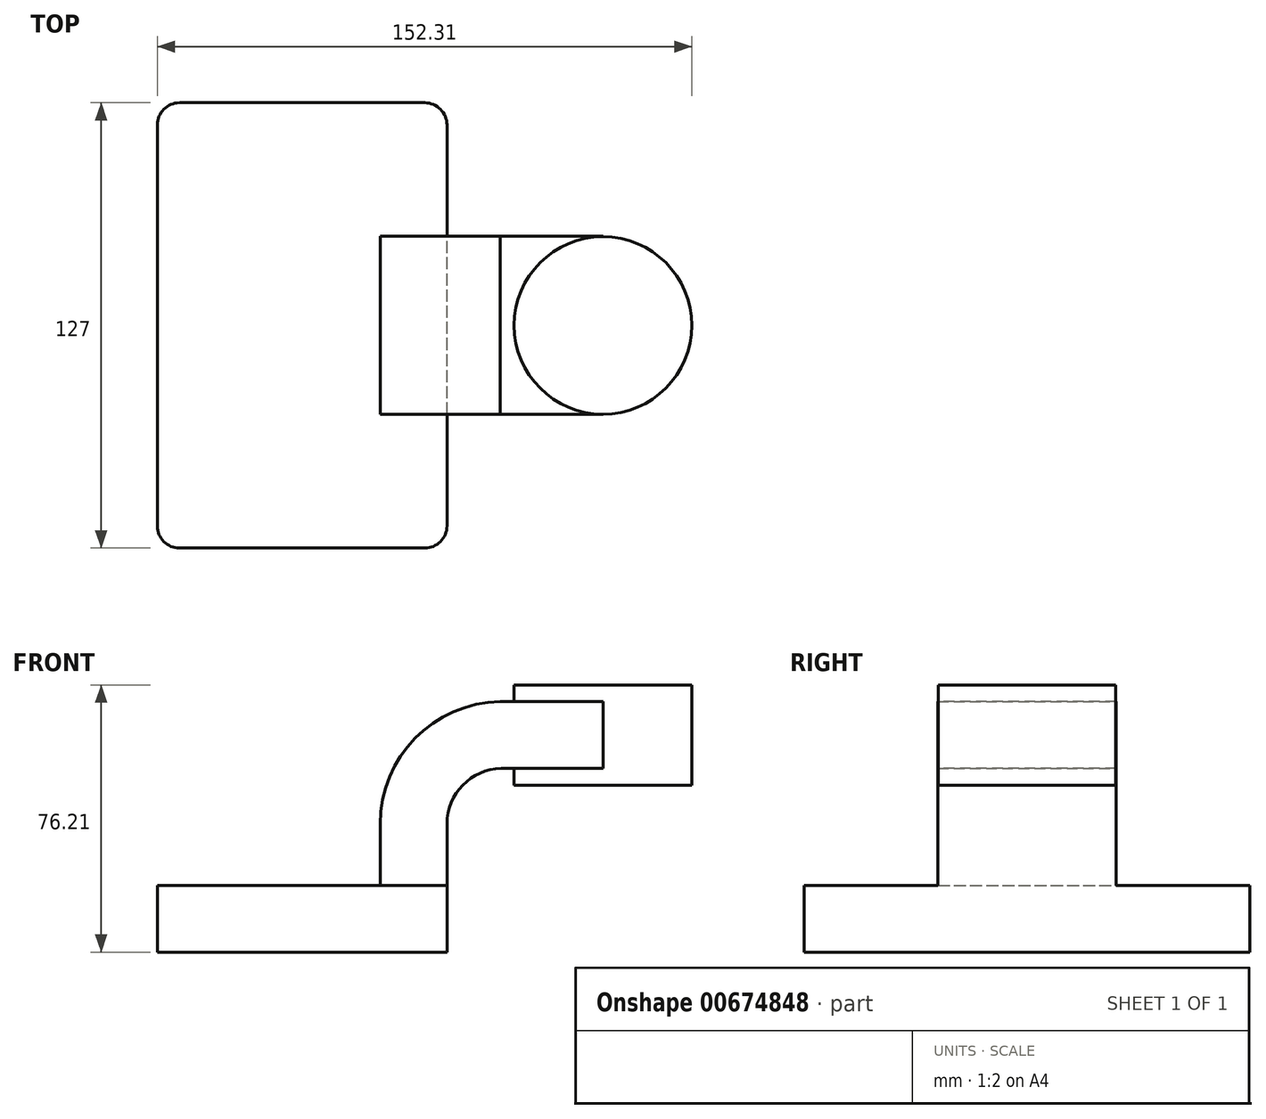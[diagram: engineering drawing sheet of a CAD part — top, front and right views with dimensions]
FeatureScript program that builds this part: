
annotation { "Feature Type Name" : "Feature", "Feature Type Description" : "" }
export const myFeature = defineFeature(function(context is Context, id is Id, definition is map)
    precondition{}
    {
        {
            var Q0;
            Q0=qCreatedBy(makeId("Front.planeOp"),FACE);
            var sketch = newSketch(context, id + "F0", { "sketchPlane" : qUnion([Q0])});
            skLineSegment(sketch, "E0.bottom", {"start": v(41.27, 9.53) * mm, "end": v(-41.28, 9.53) * mm});
            skLineSegment(sketch, "E0.top", {"start": v(41.28, -9.52) * mm, "end": v(-41.27, -9.52) * mm});
            skLineSegment(sketch, "E0.left", {"start": v(41.27, 9.53) * mm, "end": v(41.28, -9.52) * mm});
            skLineSegment(sketch, "E0.right", {"start": v(-41.28, 9.53) * mm, "end": v(-41.27, -9.52) * mm});
            skPoint(sketch, "E0.middle", {"position": v(0, 0) * mm});
            skLineSegment(sketch, "E1.bottom", {"start": v(111.04, 66.68) * mm, "end": v(60.24, 66.68) * mm});
            skLineSegment(sketch, "E1.top", {"start": v(111.04, 38.1) * mm, "end": v(60.24, 38.1) * mm});
            skLineSegment(sketch, "E1.left", {"start": v(111.04, 66.68) * mm, "end": v(111.04, 38.1) * mm});
            skLineSegment(sketch, "E1.right", {"start": v(60.24, 66.68) * mm, "end": v(60.24, 38.1) * mm});
            skPoint(sketch, "E1.middle", {"position": v(85.64, 52.39) * mm});
            skLineSegment(sketch, "E2", {"start": v(41.27, 9.53) * mm, "end": v(41.27, 27) * mm});
            skArc(sketch, "E3", {"start": v(41.27, 27) * mm, "mid": v(45.77, 38.08) * mm, "end": v(56.71, 42.88) * mm});
            skLineSegment(sketch, "E4", {"start": v(56.71, 42.88) * mm, "end": v(85.72, 42.88) * mm});
            skLineSegment(sketch, "E5.0", {"start": v(56.5, 61.93) * mm, "end": v(85.72, 61.93) * mm});
            skArc(sketch, "E5.1", {"start": v(22.22, 27) * mm, "mid": v(32.23, 51.47) * mm, "end": v(56.5, 61.93) * mm});
            skLineSegment(sketch, "E5.2", {"start": v(22.22, 9.53) * mm, "end": v(22.22, 27) * mm});
            skLineSegment(sketch, "E6.0", {"start": v(56.5, 62.23) * mm, "end": v(85.72, 62.23) * mm});
            skLineSegment(sketch, "E7", {"start": v(85.72, 62.23) * mm, "end": v(85.72, 42.88) * mm});
            skFitSpline(sketch, "E8", {"points": [v(-41.28, 9.53) * mm, v(56.5, 62.23) * mm], "startDerivative": vector(112.03, 118.7) * mm, "endDerivative": vector(97, 10.97) * mm});
            skLineSegment(sketch, "E9", {"start": v(85.72, 66.68) * mm, "end": v(85.72, 62.23) * mm});
            skLineSegment(sketch, "E10", {"start": v(85.72, 42.88) * mm, "end": v(85.72, 38.1) * mm});
            skSolve(sketch);
        }
        {
            var Q0;
            Q0=makeQuery(id+"F0.imprint","IMPRINT",FACE,{"disambiguationData":[TD([[makeQuery(id+"F0.imprint","IMPRINT",EDGE,{"derivedFrom":sQuery(id+"F0.wireOp",EDGE,"E0.top")}),-1.0]])]});
            extrude(context, id + "F1", {"entities" : qUnion([Q0]), "depth" : 127 * mm, "offsetDistance" : 25.4 * mm, "symmetric" : true});
        }
        {
            var Q0;
            {var subQ1=sQuery(id+"F0.wireOp",EDGE,"E2");Q0=makeQuery(id+"F0.imprint","IMPRINT",FACE,{"disambiguationData":[TD([[makeQuery(id+"F0.imprint","IMPRINT",EDGE,{"derivedFrom":subQ1}),1.0]])]});}
            var Q1;
            {var subQ0=sQuery(id+"F0.wireOp",EDGE,"E4");var subQ1=sQuery(id+"F0.wireOp",EDGE,"E1.right");var subQ2=makeQuery(id+"F0.imprint","INTERSECT",VERTEX,{"derivedFrom":[subQ1,subQ0]});Q1=makeQuery(id+"F0.imprint","IMPRINT",FACE,{"disambiguationData":[TD([[makeQuery(id+"F0.imprint","IMPRINT",EDGE,{"disambiguationData":[TD([[subQ2,1.0]])],"derivedFrom":subQ1}),1.0]])]});}
            extrude(context, id + "F2", {"entities" : qUnion([Q0, Q1]), "operationType" : NewBodyOperationType.ADD, "depth" : 50.8 * mm, "offsetDistance" : 25.4 * mm, "symmetric" : true});
        }
        {
            var Q0;
            {var subQ0=sQuery(id+"F0.wireOp",EDGE,"E5.1");Q0=makeQuery(id+"F0.imprint","IMPRINT",FACE,{"disambiguationData":[TD([[makeQuery(id+"F0.imprint","IMPRINT",EDGE,{"derivedFrom":subQ0}),1.0]])]});}
            extrude(context, id + "F3", {"entities" : qUnion([Q0]), "operationType" : NewBodyOperationType.ADD, "depth" : 15.88 * mm, "offsetDistance" : 25.4 * mm, "symmetric" : true});
        }
        {
            var Q0;
            {var subQ3=sQuery(id+"F0.wireOp",EDGE,"E1.left");Q0=makeQuery(id+"F0.imprint","IMPRINT",FACE,{"disambiguationData":[TD([[makeQuery(id+"F0.imprint","IMPRINT",EDGE,{"derivedFrom":subQ3}),-1.0]])]});}
            var Q1;
            Q1=sQuery(id+"F0.wireOp",EDGE,"E7");
            revolve(context, id + "F4", {"operationType" : NewBodyOperationType.ADD, "entities" : qUnion([Q0]), "axis" : qUnion([Q1]), "revolveType" : RevolveType.FULL});
        }
        {
            var Q0;
            Q0=makeQuery(id+"F1.opExtrude","CAP_EDGE",EDGE,{"disambiguationData":[OSD([sQuery(id+"F0.wireOp",EDGE,"E0.left")])],"isStart":false});
            var Q1;
            Q1=makeQuery(id+"F1.opExtrude","CAP_EDGE",EDGE,{"disambiguationData":[OSD([sQuery(id+"F0.wireOp",EDGE,"E0.left")])],"isStart":true});
            fillet(context, id + "F5", {"entities" : qUnion([Q0, Q1]), "radius" : 6.35 * mm, "tangentPropagation" : true, "allowEdgeOverflow" : false});
        }
        {
            var Q0;
            Q0=makeQuery(id+"F1.opExtrude","CAP_EDGE",EDGE,{"disambiguationData":[OSD([sQuery(id+"F0.wireOp",EDGE,"E0.right")])],"isStart":false});
            var Q1;
            Q1=makeQuery(id+"F1.opExtrude","CAP_EDGE",EDGE,{"disambiguationData":[OSD([sQuery(id+"F0.wireOp",EDGE,"E0.right")])],"isStart":true});
            fillet(context, id + "F6", {"entities" : qUnion([Q0, Q1]), "radius" : 6.35 * mm, "tangentPropagation" : true, "allowEdgeOverflow" : false});
        }
    });
